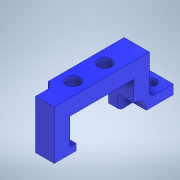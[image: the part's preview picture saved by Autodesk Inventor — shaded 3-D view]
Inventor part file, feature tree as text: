
AUTODESK INVENTOR PART (.ipt)
format: ipt  version: 2022.6 (Build 266554000, 554)  size: 212,480 bytes
history: native  units: mm
features: sketch x7, extrude x5, projected_geometry x5, hole x2, fillet x2
ambient origin geometry x8: Origin, YZ Plane, XZ Plane, XY Plane, X Axis, Y Axis, Z Axis, Center Point
bodies: Solid1 (feature_tree)
feature tree (21):
  extrude  "Extrusion1"  Depth=5.0mm
  hole  "Hole1"  [1 undecoded]
  extrude  "Extrusion2"  Depth=8.0mm
  extrude  "Extrusion3"  Depth=10.0mm
  extrude  "Extrusion4"  Depth=0.5mm
  fillet  "Fillet1"  [1 undecoded]
  extrude  "Extrusion5"  Depth=2.0mm
  fillet  "Fillet2"  Radius=2.8mm
  hole  "Hole4"  [1 undecoded]
  sketch  "Sketch1"  dims[d0=5.0mm d2=5.0mm]
  sketch  "Sketch2"  dims[d3=20.2mm d4=5.0mm]
  projected_geometry  "Projected Loop1"
  sketch  "Sketch4"  dims[d5=8.0mm d6=0.0mm d7=3.9mm]
  projected_geometry  "Projected Loop2"
  sketch  "Sketch5"  dims[d8=10.0mm]
  projected_geometry  "Projected Loop3"
  sketch  "Sketch6"  dims[d9=4.3mm d10=6.0mm d11=4.0mm d12=2.0mm d13=90.0deg d14=10.0mm d15=20.594885mm d16=10.5mm]
  projected_geometry  "Projected Loop4"
  sketch  "Sketch9"  dims[d19=5.2mm d20=0.5mm d21=0.0mm d22=0.0mm]
  sketch  "Sketch10"  dims[d23=2.0mm d24=2.0mm d25=2.8mm d26=4.0mm d28=3.0mm d29=1.5mm d30=0.0mm d33=3.0mm d34=0.0mm d36=1.5mm d59=7.5mm d60=15.0mm d63=3.5mm d64=8.0mm d65=3.0mm d66=0.0mm d67=2.0mm d69=3.4mm d70=6.0mm d71=4.0mm d72=2.0mm d73=90.0deg d74=10.0mm d75=20.594885mm d76=3.0mm d77=4.0mm]
  projected_geometry  "Projected Loop9"
note: 3 required parameter values undecoded (feature->parameter linkage not recoverable at this tier; creation-order binding heuristic only, values carry confidence <= 0.55)
